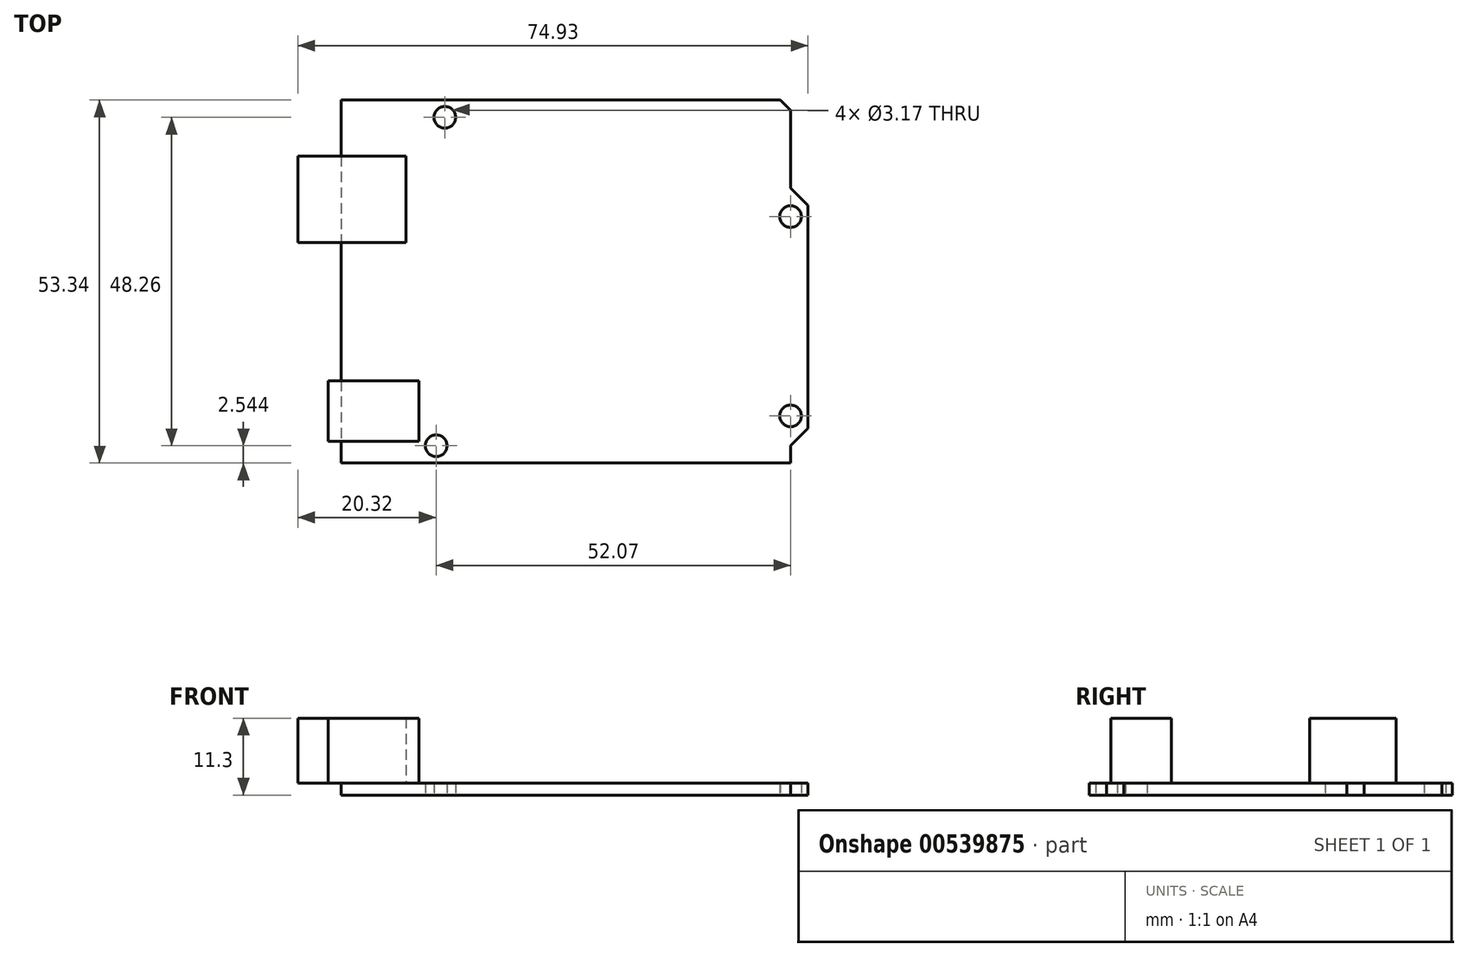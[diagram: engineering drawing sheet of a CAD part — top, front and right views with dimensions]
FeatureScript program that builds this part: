
annotation { "Feature Type Name" : "Feature", "Feature Type Description" : "" }
export const myFeature = defineFeature(function(context is Context, id is Id, definition is map)
    precondition{}
    {
        {
            var Q0;
            Q0=qCreatedBy(makeId("Top.planeOp"),FACE);
            var sketch = newSketch(context, id + "F0", { "sketchPlane" : qUnion([Q0])});
            skLineSegment(sketch, "E0", {"start": v(-66.04, 43.94) * mm, "end": v(-66.04, -9.4) * mm});
            skLineSegment(sketch, "E1", {"start": v(-66.04, -9.4) * mm, "end": v(0, -9.4) * mm});
            skLineSegment(sketch, "E2", {"start": v(0, -9.4) * mm, "end": v(0, -6.86) * mm});
            skLineSegment(sketch, "E3", {"start": v(0, -6.86) * mm, "end": v(2.54, -4.32) * mm});
            skLineSegment(sketch, "E4", {"start": v(0, 42.42) * mm, "end": v(0, 30.99) * mm});
            skLineSegment(sketch, "E5", {"start": v(0, 30.99) * mm, "end": v(2.54, 28.45) * mm});
            skLineSegment(sketch, "E6", {"start": v(-50.8, 43.94) * mm, "end": v(-50.8, 41.4) * mm});
            skLineSegment(sketch, "E7", {"start": v(-50.8, 41.4) * mm, "end": v(-66.04, 41.4) * mm});
            skCircle(sketch, "E8", {"center": v(-50.8, 41.4) * mm, "radius": 1.59 * mm});
            skLineSegment(sketch, "E9", {"start": v(-66.04, -6.86) * mm, "end": v(-52.07, -6.86) * mm});
            skLineSegment(sketch, "E10", {"start": v(-52.07, -6.86) * mm, "end": v(-52.07, -9.4) * mm});
            skCircle(sketch, "E11", {"center": v(-52.07, -6.86) * mm, "radius": 1.59 * mm});
            skLineSegment(sketch, "E12", {"start": v(2.54, 28.45) * mm, "end": v(2.54, -4.32) * mm});
            skLineSegment(sketch, "E13", {"start": v(-66.04, 43.94) * mm, "end": v(-1.52, 43.94) * mm});
            skLineSegment(sketch, "E14", {"start": v(-1.52, 43.94) * mm, "end": v(0, 42.42) * mm});
            skCircle(sketch, "E15", {"center": v(0, -2.47) * mm, "radius": 1.59 * mm});
            skCircle(sketch, "E16", {"center": v(0, 26.82) * mm, "radius": 1.59 * mm});
            skPoint(sketch, "E17.end.orphan", {"position": v(2.54, 30.6) * mm});
            skSolve(sketch);
        }
        {
            var Q0;
            Q0 = qSketchRegion(id + "F0", true);
            extrude(context, id + "F1", {"entities" : qUnion([Q0]), "depth" : 1.78 * mm, "offsetDistance" : 25.4 * mm});
        }
        {
            var Q0;
            Q0=makeQuery(id+"F1.opExtrude","CAP_FACE",FACE,{"disambiguationData":[OSD([sQuery(id+"F0.wireOp",EDGE,"E0"),sQuery(id+"F0.wireOp",EDGE,"E1"),sQuery(id+"F0.wireOp",EDGE,"E4"),sQuery(id+"F0.wireOp",EDGE,"E5"),sQuery(id+"F0.wireOp",EDGE,"E8"),sQuery(id+"F0.wireOp",EDGE,"E11"),sQuery(id+"F0.wireOp",EDGE,"E12"),sQuery(id+"F0.wireOp",EDGE,"E13"),sQuery(id+"F0.wireOp",EDGE,"E14"),sQuery(id+"F0.wireOp",EDGE,"E15"),sQuery(id+"F0.wireOp",EDGE,"E16"),sQuery(id+"F0.wireOp",EDGE,"VkfS3Nqm-0NbJ-U0JU-8MQo-YuWy7RmPPbee"),sQuery(id+"F0.wireOp",EDGE,"ZKsa5orM-EeOH-iKZC-BkG5-DrPSswukk0RC")])],"isStart":false});
            var sketch = newSketch(context, id + "F2", { "sketchPlane" : qUnion([Q0])});
            skLineSegment(sketch, "E18", {"start": v(-54.6, -6.22) * mm, "end": v(-54.6, -9.4) * mm});
            skLineSegment(sketch, "E19", {"start": v(-54.6, -6.22) * mm, "end": v(-54.6, 2.67) * mm});
            skLineSegment(sketch, "E20", {"start": v(-54.6, 2.67) * mm, "end": v(-67.95, 2.67) * mm});
            skLineSegment(sketch, "E21", {"start": v(-67.95, 2.67) * mm, "end": v(-67.95, -6.22) * mm});
            skLineSegment(sketch, "E22", {"start": v(-67.95, -6.22) * mm, "end": v(-54.6, -6.22) * mm});
            skLineSegment(sketch, "E23", {"start": v(-66.04, 22.99) * mm, "end": v(-56.52, 22.99) * mm});
            skLineSegment(sketch, "E24", {"start": v(-56.52, 22.99) * mm, "end": v(-56.52, 35.69) * mm});
            skLineSegment(sketch, "E25", {"start": v(-56.52, 35.69) * mm, "end": v(-72.4, 35.69) * mm});
            skLineSegment(sketch, "E26", {"start": v(-72.4, 35.69) * mm, "end": v(-72.4, 22.99) * mm});
            skLineSegment(sketch, "E27", {"start": v(-72.4, 22.99) * mm, "end": v(-66.04, 22.99) * mm});
            skSolve(sketch);
        }
        {
            var Q0;
            Q0 = qSketchRegion(id + "F2", true);
            extrude(context, id + "F3", {"entities" : qUnion([Q0]), "depth" : 9.52 * mm, "offsetDistance" : 25.4 * mm});
        }
    });
